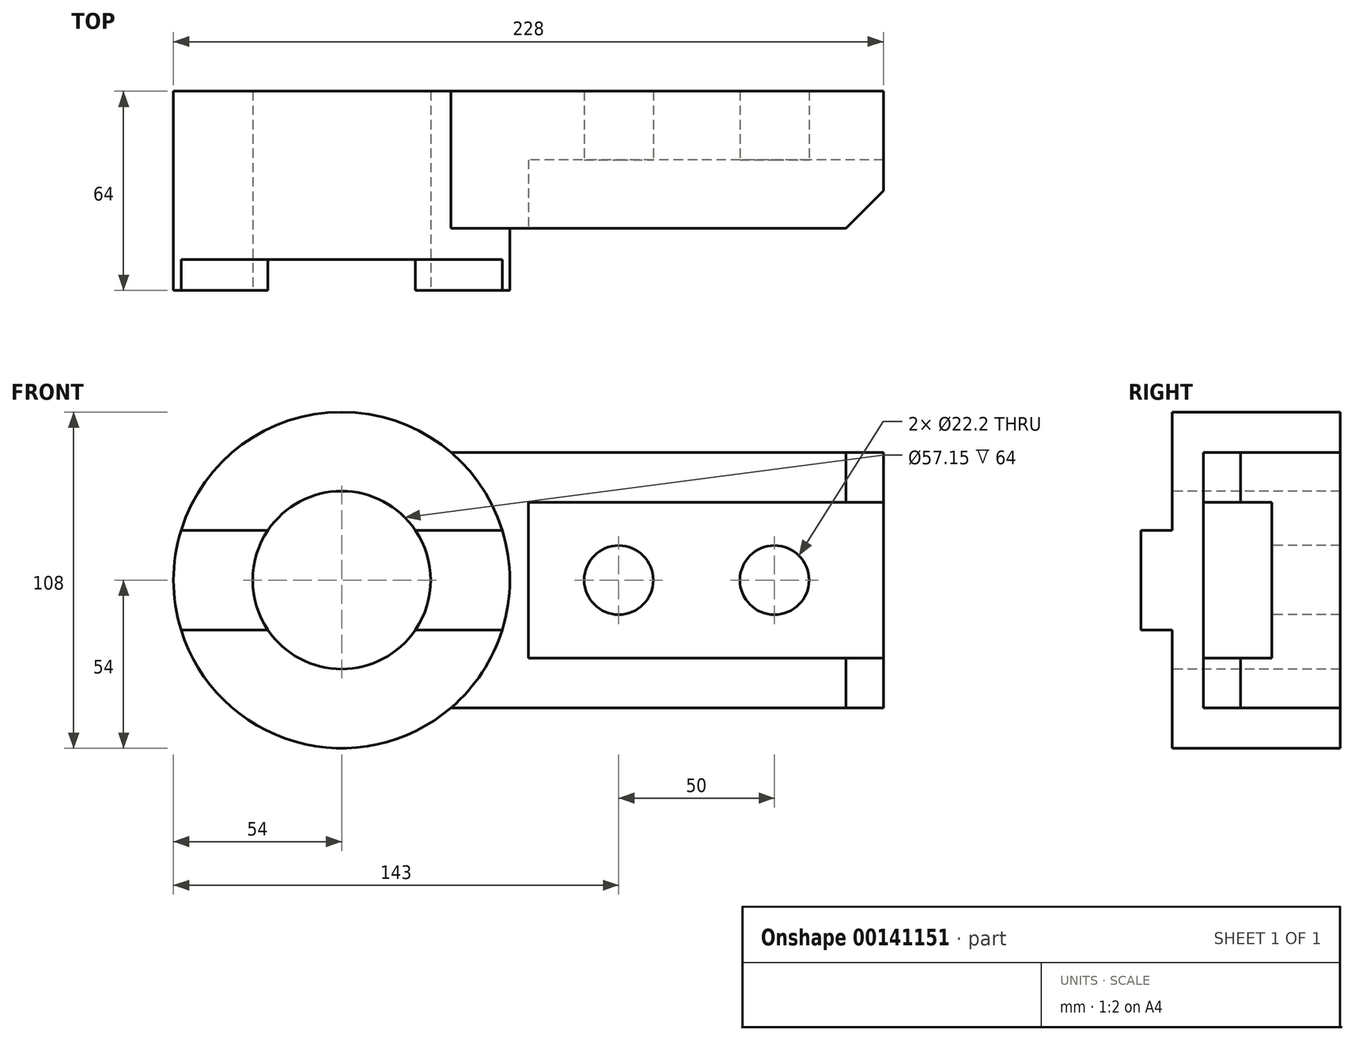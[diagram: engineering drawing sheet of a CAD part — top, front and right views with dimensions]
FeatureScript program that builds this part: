
annotation { "Feature Type Name" : "Feature", "Feature Type Description" : "" }
export const myFeature = defineFeature(function(context is Context, id is Id, definition is map)
    precondition{}
    {
        {
            var Q0;
            Q0=qCreatedBy(makeId("Front.planeOp"),FACE);
            var sketch = newSketch(context, id + "F0", { "sketchPlane" : qUnion([Q0])});
            skCircle(sketch, "E0", {"center": v(0, 0) * mm, "radius": 28.57 * mm});
            skCircle(sketch, "E1", {"center": v(0, 0) * mm, "radius": 54 * mm});
            skSolve(sketch);
        }
        {
            var Q0;
            Q0 = qSketchRegion(id + "F0", true);
            extrude(context, id + "F1", {"entities" : qUnion([Q0]), "oppositeDirection" : true, "depth" : 54 * mm});
        }
        {
            var Q0;
            Q0=makeQuery(id+"F1.opExtrude","CAP_FACE",FACE,{"disambiguationData":[OSD([sQuery(id+"F0.wireOp",EDGE,"E0"),sQuery(id+"F0.wireOp",EDGE,"E1")])],"isStart":true});
            var sketch = newSketch(context, id + "F2", { "sketchPlane" : qUnion([Q0])});
            skLineSegment(sketch, "E2", {"start": v(-51.58, 16) * mm, "end": v(-23.68, 16) * mm});
            skLineSegment(sketch, "E3", {"start": v(-51.58, -16) * mm, "end": v(-23.68, -16) * mm});
            skArc(sketch, "E4.0", {"start": v(-51.58, 16) * mm, "mid": v(-54, 0) * mm, "end": v(-51.58, -16) * mm});
            skArc(sketch, "E5.0", {"start": v(-23.68, 16) * mm, "mid": v(-28.58, 0) * mm, "end": v(-23.68, -16) * mm});
            skArc(sketch, "E6.trimOffspring", {"start": v(51.58, -16) * mm, "mid": v(54, 0) * mm, "end": v(51.58, 16) * mm});
            skLineSegment(sketch, "E7.trimOffspring", {"start": v(23.68, 16) * mm, "end": v(51.58, 16) * mm});
            skLineSegment(sketch, "E8.trimOffspring", {"start": v(23.68, -16) * mm, "end": v(51.58, -16) * mm});
            skArc(sketch, "E9.trimOffspring", {"start": v(23.68, -16) * mm, "mid": v(28.57, 0) * mm, "end": v(23.68, 16) * mm});
            skSolve(sketch);
        }
        {
            var Q0;
            Q0 = qSketchRegion(id + "F2", true);
            extrude(context, id + "F3", {"entities" : qUnion([Q0]), "operationType" : NewBodyOperationType.ADD, "depth" : 10 * mm});
        }
        {
            var Q0;
            Q0=makeQuery(id+"F1.opExtrude","CAP_FACE",FACE,{"disambiguationData":[OSD([sQuery(id+"F0.wireOp",EDGE,"E0"),sQuery(id+"F0.wireOp",EDGE,"E1")])],"isStart":false});
            var sketch = newSketch(context, id + "F4", { "sketchPlane" : qUnion([Q0])});
            skArc(sketch, "E10.0", {"start": v(-35.14, 41) * mm, "mid": v(-54, 0) * mm, "end": v(-35.14, -41) * mm});
            skLineSegment(sketch, "E11", {"start": v(-35.14, 41) * mm, "end": v(-174, 41) * mm});
            skLineSegment(sketch, "E12", {"start": v(-174, 41) * mm, "end": v(-174, -41) * mm});
            skLineSegment(sketch, "E13", {"start": v(-174, -41) * mm, "end": v(-35.14, -41) * mm});
            skSolve(sketch);
        }
        {
            var Q0;
            Q0 = qSketchRegion(id + "F4", true);
            extrude(context, id + "F5", {"entities" : qUnion([Q0]), "operationType" : NewBodyOperationType.ADD, "oppositeDirection" : true, "depth" : 44 * mm});
        }
        {
            var Q0;
            Q0=makeQuery(id+"F5.opExtrude","CAP_FACE",FACE,{"disambiguationData":[OSD([sQuery(id+"F4.wireOp",EDGE,"E10.0"),sQuery(id+"F4.wireOp",EDGE,"E11"),sQuery(id+"F4.wireOp",EDGE,"E12"),sQuery(id+"F4.wireOp",EDGE,"E13")])],"isStart":false});
            var sketch = newSketch(context, id + "F6", { "sketchPlane" : qUnion([Q0])});
            skLineSegment(sketch, "E14", {"start": v(174, 25) * mm, "end": v(60, 25) * mm});
            skLineSegment(sketch, "E15", {"start": v(60, 25) * mm, "end": v(60, -25) * mm});
            skLineSegment(sketch, "E16", {"start": v(60, -25) * mm, "end": v(174, -25) * mm});
            skLineSegment(sketch, "E17", {"start": v(174, -25) * mm, "end": v(174, 25) * mm});
            skSolve(sketch);
        }
        {
            var Q0;
            Q0 = qSketchRegion(id + "F6", true);
            extrude(context, id + "F7", {"entities" : qUnion([Q0]), "operationType" : NewBodyOperationType.REMOVE, "oppositeDirection" : true, "depth" : 22 * mm});
        }
        {
            var Q0;
            Q0=makeQuery(id+"F7.boolean.opBoolean","COPY",FACE,{"derivedFrom":makeQuery(id+"F7.opExtrude","CAP_FACE",FACE,{"disambiguationData":[OSD([sQuery(id+"F6.wireOp",EDGE,"E14"),sQuery(id+"F6.wireOp",EDGE,"E15"),sQuery(id+"F6.wireOp",EDGE,"E16"),sQuery(id+"F6.wireOp",EDGE,"E17")])],"isStart":false})});
            var sketch = newSketch(context, id + "F8", { "sketchPlane" : qUnion([Q0])});
            skCircle(sketch, "E18", {"center": v(89, 0) * mm, "radius": 11.1 * mm});
            skCircle(sketch, "E19", {"center": v(139, 0) * mm, "radius": 11.1 * mm});
            skSolve(sketch);
        }
        {
            var Q0;
            Q0 = qSketchRegion(id + "F8", true);
            extrude(context, id + "F9", {"entities" : qUnion([Q0]), "operationType" : NewBodyOperationType.REMOVE, "endBound" : BoundingType.THROUGH_ALL, "oppositeDirection" : true, "depth" : 25 * mm});
        }
        {
            var Q0;
            Q0=makeQuery(id+"F5.opExtrude","SWEPT_FACE",FACE,{"disambiguationData":[OSD([sQuery(id+"F4.wireOp",EDGE,"E11")])]});
            var sketch = newSketch(context, id + "F10", { "sketchPlane" : qUnion([Q0])});
            skLineSegment(sketch, "E20", {"start": v(174, 22) * mm, "end": v(162, 10) * mm});
            skLineSegment(sketch, "E21", {"start": v(162, 10) * mm, "end": v(174, 10) * mm});
            skLineSegment(sketch, "E22", {"start": v(174, 10) * mm, "end": v(174, 22) * mm});
            skSolve(sketch);
        }
        {
            var Q0;
            Q0 = qSketchRegion(id + "F10", true);
            extrude(context, id + "F11", {"entities" : qUnion([Q0]), "operationType" : NewBodyOperationType.REMOVE, "endBound" : BoundingType.THROUGH_ALL, "oppositeDirection" : true, "depth" : 25 * mm});
        }
    });
